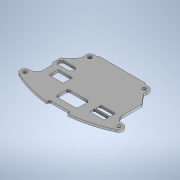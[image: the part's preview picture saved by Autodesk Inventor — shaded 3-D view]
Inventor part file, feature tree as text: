
AUTODESK INVENTOR PART (.ipt)
format: ipt  version: 2020 (Build 240168000, 168)  size: 664,576 bytes
history: native  units: mm
features: extrude x4, sketch x3, other x2, projected_geometry x2, chamfer x1, fillet x1
ambient origin geometry x8: Origin, YZ Plane, XZ Plane, XY Plane, X Axis, Y Axis, Z Axis, Center Point
bodies: Body1 (feature_tree)
feature tree (13):
  other  "Твердое тело1"
  other  "РабПлоскость1"
  sketch  "Эскиз1"
  extrude  "Выдавливание1"  Depth=3.0mm
  extrude  "Выдавливание2"  Depth=7.0mm
  chamfer  "Фаска1"  Distance=4.75mm
  fillet  "Сопряжение1"  Radius=4.75mm
  sketch  "Эскиз2"
  extrude  "Выдавливание3"  Depth=1.0mm
  extrude  "Выдавливание4"  Depth=1.0mm
  projected_geometry  "Спроецированная петля1"
  projected_geometry  "Спроецированная петля18"
  sketch  "Эскиз3"
